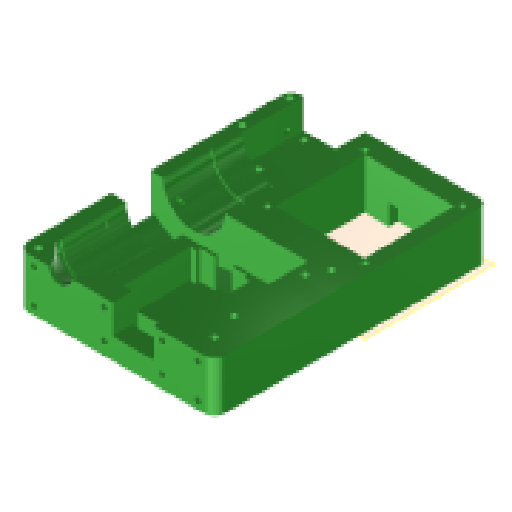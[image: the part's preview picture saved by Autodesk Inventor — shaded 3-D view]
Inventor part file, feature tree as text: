
AUTODESK INVENTOR PART (.ipt)
format: ipt  version: 2024.1 (Build 281209000, 209)  size: 500,736 bytes
history: native  units: mm
features: reference x21, sketch x11, other x9, projected_geometry x7, extrude x6, hole x4, plane x2, fillet x2, revolve x1
ambient origin geometry x8: Origin, YZ Plane, XZ Plane, XY Plane, X Axis, Y Axis, Z Axis, Center Point
bodies: Volumenkörper1 (feature_tree)
feature tree (63):
  plane  "Arbeitsebene1"
  plane  "Arbeitsebene2"
  extrude  "Extrusion1"  Depth=2.8mm
  revolve  "Umdrehung1"
  extrude  "Extrusion2"  Depth=2.8mm
  extrude  "Extrusion3"  Depth=95.0mm
  extrude  "Extrusion4"  Depth=50.0mm TaperAngle=0.0deg
  hole  "Bohrung1"  [1 undecoded]
  hole  "Bohrung2"  [1 undecoded]
  hole  "Bohrung4"  [1 undecoded]
  fillet  "Rundung1"  Radius=12.0mm
  extrude  "Extrusion6"  Depth=14.0mm
  extrude  "Extrusion7"  Depth=1.0mm TaperAngle=0.0deg
  fillet  "Rundung2"  Radius=0.3mm
  hole  "Bohrung6"  [1 undecoded]
  sketch  "Skizze1"  dims[d0=0.5mm d1=2.8mm]
  reference  "Referenz1"
  reference  "Referenz2"
  reference  "Referenz3"
  reference  "Referenz4"
  reference  "Referenz5"
  reference  "Referenz6"
  reference  "Referenz7"
  reference  "Referenz8"
  reference  "Referenz9"
  reference  "Referenz10"
  sketch  "Skizze2"  dims[d2=2.8mm d3=2.8mm]
  projected_geometry  "Projizierte Kontur1"
  reference  "Referenz11"
  reference  "Referenz12"
  sketch  "Skizze3"  dims[d4=2.8mm d5=95.0mm]
  reference  "Referenz13"
  reference  "Referenz14"
  reference  "Referenz15"
  reference  "Referenz16"
  sketch  "Skizze4"  dims[d6=132.0mm d7=50.0mm d8=0.0mm]
  reference  "Referenz17"
  reference  "Referenz18"
  sketch  "Skizze5"  dims[d9=0.25mm d10=360.0deg]
  projected_geometry  "Projizierte Kontur2"
  reference  "Referenz19"
  reference  "Referenz20"
  sketch  "Skizze6"  dims[d11=20.0mm d12=0.5mm]
  projected_geometry  "Projizierte Kontur3"
  sketch  "Skizze8"  dims[d13=0.5mm d14=14.1mm d15=0.0mm d16=12.0mm]
  projected_geometry  "Projizierte Kontur4"
  sketch  "Skizze10"  dims[d17=11.0mm d18=14.0mm]
  projected_geometry  "Projizierte Kontur5"
  sketch  "Skizze12"  dims[d19=18.0mm d20=0.0mm d21=1.0mm d22=0.0mm d23=0.3mm]
  projected_geometry  "Projizierte Kontur7"
  sketch  "Skizze13"  dims[d24=14.3mm d25=0.0mm d26=10.0mm]
  projected_geometry  "Projizierte Kontur8"
  sketch  "Skizze14"  dims[d27=3.3mm d28=6.0mm d29=6.5mm d30=8.0mm d31=90.0deg d32=8.0mm d33=20.594885mm d34=3.0mm d35=3.0mm d41=31.15mm d43=2.8mm d44=6.0mm d45=6.5mm d46=8.0mm d47=90.0deg d48=12.0mm d49=20.594885mm d58=2.8mm d59=6.0mm d60=4.0mm d61=2.0mm d62=90.0deg d63=12.0mm d64=20.594885mm d74=1.0mm d75=2.25mm d76=2.0mm d77=7.0mm d78=0.0mm d79=0.0mm d80=20.0mm d81=9.0mm d82=10.0mm d83=0.0mm d84=5.0mm d85=2.8mm d86=6.0mm d87=4.0mm d88=2.0mm d89=90.0deg d90=12.0mm d91=20.594885mm]
  reference  "Referenz25"
  other  "Assembly_Planktoscope_Uc2version_V1.iam"
  other  "00_NEMA17_Perestalticpump_Adapter:1"
  other  "00_NEMA_17:1"
  other  "00_HIKCamera_MV-CE060-10UMUC:1"
  other  "00_Microscope_Slide:2"
  other  "00_CCTV_Lens_Hikvision_50mm_2.8:1"
  other  "00_NEMA11:3"
  other  "60_Planktoscope_Wallboxmoutingplate:1"
  other  "Assembly_Planktoscope_Uc2version_V!.iam"
note: 4 required parameter values undecoded (feature->parameter linkage not recoverable at this tier; creation-order binding heuristic only, values carry confidence <= 0.55)
